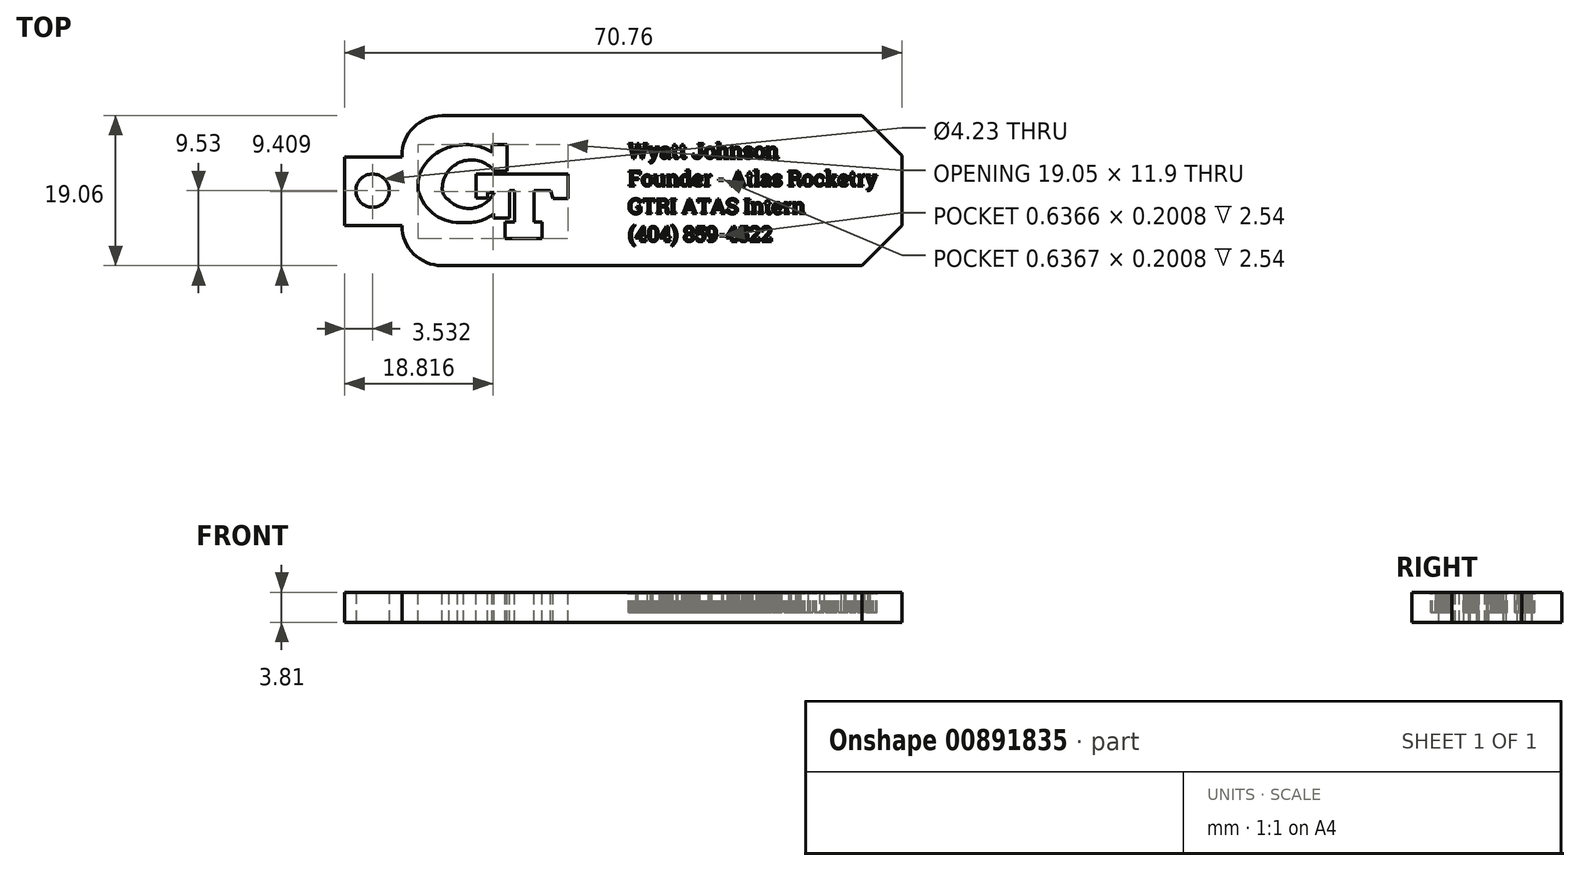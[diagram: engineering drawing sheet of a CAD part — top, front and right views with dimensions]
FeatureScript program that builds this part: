
annotation { "Feature Type Name" : "Feature", "Feature Type Description" : "" }
export const myFeature = defineFeature(function(context is Context, id is Id, definition is map)
    precondition{}
    {
        {
            var Q0;
            Q0=qCreatedBy(makeId("Top.planeOp"),FACE);
            var sketch = newSketch(context, id + "F0", { "sketchPlane" : qUnion([Q0])});
            skLineSegment(sketch, "E0.bottom", {"start": v(31.75, -9.52) * mm, "end": v(-31.75, -9.53) * mm});
            skLineSegment(sketch, "E0.top", {"start": v(31.75, 9.53) * mm, "end": v(-31.75, 9.53) * mm});
            skLineSegment(sketch, "E0.left", {"start": v(31.75, -9.53) * mm, "end": v(31.75, 9.53) * mm});
            skLineSegment(sketch, "E0.right", {"start": v(-31.75, -9.53) * mm, "end": v(-31.75, 9.53) * mm});
            skPoint(sketch, "E0.middle", {"position": v(0, 0) * mm});
            skSolve(sketch);
        }
        {
            var Q0;
            Q0 = qSketchRegion(id + "F0", true);
            var Q1;
            Q1 = qSketchRegion(id + "F8", true);
            extrude(context, id + "F1", {"entities" : qUnion([Q0, Q1]), "depth" : 3.8 * mm, "offsetDistance" : 25.4 * mm});
        }
        {
            var Q0;
            Q0=qCreatedBy(makeId("Top.planeOp"),FACE);
            var sketch = newSketch(context, id + "F2", { "sketchPlane" : qUnion([Q0])});
            skLineSegment(sketch, "E1", {"start": v(-20.28, 5.83) * mm, "end": v(-20.28, 4.88) * mm});
            skPoint(sketch, "E1.startSnap0", {"position": v(-20.28, 6.07) * mm});
            skArc(sketch, "E2", {"start": v(-28.9, 3.23) * mm, "mid": v(-29.6, 1.7) * mm, "end": v(-29.67, 0) * mm});
            skArc(sketch, "E3", {"start": v(-24.69, 5.74) * mm, "mid": v(-27.06, 4.94) * mm, "end": v(-28.9, 3.23) * mm});
            skArc(sketch, "E4", {"start": v(-20.28, 4.88) * mm, "mid": v(-22.4, 5.71) * mm, "end": v(-24.69, 5.74) * mm});
            skLineSegment(sketch, "E5", {"start": v(-20.28, 5.83) * mm, "end": v(-18.38, 5.83) * mm});
            skLineSegment(sketch, "E6", {"start": v(-18.38, 5.83) * mm, "end": v(-18.38, 2.5) * mm});
            skLineSegment(sketch, "E7", {"start": v(-18.38, 2.5) * mm, "end": v(-20.03, 2.5) * mm});
            skArc(sketch, "E8", {"start": v(-26.63, 0.26) * mm, "mid": v(-26.4, -0.6) * mm, "end": v(-25.78, -1.22) * mm});
            skArc(sketch, "E9", {"start": v(-20.03, 2.5) * mm, "mid": v(-24.12, 3.7) * mm, "end": v(-26.63, 0.26) * mm});
            skArc(sketch, "E10", {"start": v(-25.78, -1.22) * mm, "mid": v(-22.64, -2.22) * mm, "end": v(-20.03, -0.22) * mm});
            skLineSegment(sketch, "E11", {"start": v(-22.33, -0.97) * mm, "end": v(-22.33, 2.11) * mm});
            skLineSegment(sketch, "E12", {"start": v(-22.33, 2.11) * mm, "end": v(-10.67, 2.11) * mm});
            skLineSegment(sketch, "E13", {"start": v(-10.67, 2.11) * mm, "end": v(-10.67, -1.01) * mm});
            skLineSegment(sketch, "E14", {"start": v(-10.67, -1.01) * mm, "end": v(-12.54, -1.01) * mm});
            skLineSegment(sketch, "E15", {"start": v(-12.54, -1.01) * mm, "end": v(-12.9, 0) * mm});
            skLineSegment(sketch, "E16", {"start": v(-14.96, 0) * mm, "end": v(-14.96, -3.99) * mm});
            skLineSegment(sketch, "E17", {"start": v(-14.96, -3.99) * mm, "end": v(-13.96, -3.99) * mm});
            skLineSegment(sketch, "E18", {"start": v(-13.96, -3.99) * mm, "end": v(-13.96, -6.07) * mm});
            skLineSegment(sketch, "E19", {"start": v(-13.96, -6.07) * mm, "end": v(-18.64, -6.07) * mm});
            skLineSegment(sketch, "E20", {"start": v(-18.64, -6.07) * mm, "end": v(-18.64, -3.99) * mm});
            skLineSegment(sketch, "E21", {"start": v(-18.64, -3.99) * mm, "end": v(-17.44, -3.99) * mm});
            skLineSegment(sketch, "E22", {"start": v(-17.44, -3.99) * mm, "end": v(-17.44, 0) * mm});
            skLineSegment(sketch, "E23", {"start": v(-18.06, 0) * mm, "end": v(-18.06, -3.46) * mm});
            skLineSegment(sketch, "E24", {"start": v(-18.06, -3.46) * mm, "end": v(-20.09, -3.46) * mm});
            skLineSegment(sketch, "E25", {"start": v(-20.09, -3.46) * mm, "end": v(-20.09, -2.93) * mm});
            skArc(sketch, "E26", {"start": v(-29.67, 0) * mm, "mid": v(-27.53, -3.1) * mm, "end": v(-23.9, -4.05) * mm});
            skArc(sketch, "E27", {"start": v(-23.9, -4.05) * mm, "mid": v(-21.88, -3.86) * mm, "end": v(-20.09, -2.93) * mm});
            skLineSegment(sketch, "E28", {"start": v(-20.03, -0.22) * mm, "end": v(-20.84, -0.22) * mm});
            skLineSegment(sketch, "E29", {"start": v(-20.84, -0.22) * mm, "end": v(-20.84, -0.91) * mm});
            skLineSegment(sketch, "E30", {"start": v(-20.84, -0.91) * mm, "end": v(-22.33, -0.97) * mm});
            skLineSegment(sketch, "E31", {"start": v(-18.06, 0) * mm, "end": v(-17.44, 0) * mm});
            skLineSegment(sketch, "E32", {"start": v(-14.96, 0) * mm, "end": v(-12.9, 0) * mm});
            skSolve(sketch);
        }
        {
            var Q0;
            Q0 = qSketchRegion(id + "F2", true);
            extrude(context, id + "F3", {"entities" : qUnion([Q0]), "operationType" : NewBodyOperationType.REMOVE, "endBound" : BoundingType.THROUGH_ALL, "oppositeDirection" : true, "depth" : 25.4 * mm, "offsetDistance" : 25.4 * mm, "hasSecondDirection" : true, "secondDirectionOppositeDirection" : false, "secondDirectionDepth" : 25.4 * mm});
        }
        {
            var Q0;
            Q0=makeQuery(id+"F1.opExtrude","SWEPT_EDGE",EDGE,{"disambiguationData":[OSD([sQuery(id+"F0.wireOp",EDGE,"E0.bottom"),sQuery(id+"F0.wireOp",EDGE,"E0.left")])]});
            var Q1;
            Q1=makeQuery(id+"F1.opExtrude","SWEPT_EDGE",EDGE,{"disambiguationData":[OSD([sQuery(id+"F0.wireOp",EDGE,"E0.top"),sQuery(id+"F0.wireOp",EDGE,"E0.left")])]});
            chamfer(context, id + "F4", {"entities" : qUnion([Q0, Q1]), "width" : 5.08 * mm, "tangentPropagation" : true});
        }
        {
            var Q0;
            Q0=makeQuery(id+"F1.opExtrude","SWEPT_EDGE",EDGE,{"disambiguationData":[OSD([sQuery(id+"F0.wireOp",EDGE,"E0.bottom"),sQuery(id+"F0.wireOp",EDGE,"E0.right")])]});
            var Q1;
            Q1=makeQuery(id+"F1.opExtrude","SWEPT_EDGE",EDGE,{"disambiguationData":[OSD([sQuery(id+"F0.wireOp",EDGE,"E0.top"),sQuery(id+"F0.wireOp",EDGE,"E0.right")])]});
            fillet(context, id + "F5", {"entities" : qUnion([Q0, Q1]), "radius" : 5.08 * mm, "tangentPropagation" : true, "allowEdgeOverflow" : false});
        }
        {
            var Q0;
            Q0=makeQuery(id+"F1.opExtrude","CAP_FACE",FACE,{"disambiguationData":[OSD([sQuery(id+"F0.wireOp",EDGE,"E0.bottom"),sQuery(id+"F0.wireOp",EDGE,"E0.top"),sQuery(id+"F0.wireOp",EDGE,"E0.left"),sQuery(id+"F0.wireOp",EDGE,"E0.right")])],"isStart":false});
            var sketch = newSketch(context, id + "F6", { "sketchPlane" : qUnion([Q0])});
            skText(sketch, "E33", { "text": "Wyatt Johnson \nFounder - Atlas Rocketry \nGTRI ATAS Intern\n(404) 859-4522", "fontName": "RobotoSlab-Regular.ttf"});
            const initialGuessF6  = {"E33": [-0.003, 0.0041, 1, 0, 0.00192]};
            skSetInitialGuess(sketch, initialGuessF6);
            skSolve(sketch);
        }
        {
            var Q0;
            Q0 = qSketchRegion(id + "F6", true);
            extrude(context, id + "F7", {"entities" : qUnion([Q0]), "operationType" : NewBodyOperationType.REMOVE, "oppositeDirection" : true, "depth" : 2.54 * mm, "offsetDistance" : 25.4 * mm});
        }
        {
            var Q0;
            Q0=makeQuery(id+"F1.opExtrude","CAP_FACE",FACE,{"disambiguationData":[OSD([sQuery(id+"F0.wireOp",EDGE,"E0.bottom"),sQuery(id+"F0.wireOp",EDGE,"E0.top"),sQuery(id+"F0.wireOp",EDGE,"E0.left"),sQuery(id+"F0.wireOp",EDGE,"E0.right")])],"isStart":true});
            var sketch = newSketch(context, id + "F8", { "sketchPlane" : qUnion([Q0])});
            skLineSegment(sketch, "E34.bottom", {"start": v(-31.75, 4.45) * mm, "end": v(-39.01, 4.45) * mm});
            skLineSegment(sketch, "E34.top", {"start": v(-31.75, -4.24) * mm, "end": v(-39.01, -4.24) * mm});
            skLineSegment(sketch, "E34.left", {"start": v(-31.75, 4.45) * mm, "end": v(-31.75, -4.24) * mm});
            skLineSegment(sketch, "E34.right", {"start": v(-39.01, 4.45) * mm, "end": v(-39.01, -4.24) * mm});
            skSolve(sketch);
        }
        {
            var Q0;
            Q0 = qSketchRegion(id + "F8", true);
            extrude(context, id + "F9", {"entities" : qUnion([Q0]), "operationType" : NewBodyOperationType.ADD, "depth" : 0 * mm, "offsetDistance" : 25.4 * mm, "hasSecondDirection" : true, "secondDirectionOppositeDirection" : true, "secondDirectionDepth" : 3.8 * mm});
        }
        {
            var Q0;
            Q0=makeQuery(id+"F9.boolean.opBoolean","MERGE",FACE,{"derivedFrom":[makeQuery(id+"F1.opExtrude","CAP_FACE",FACE,{"disambiguationData":[OSD([sQuery(id+"F0.wireOp",EDGE,"E0.bottom"),sQuery(id+"F0.wireOp",EDGE,"E0.top"),sQuery(id+"F0.wireOp",EDGE,"E0.left"),sQuery(id+"F0.wireOp",EDGE,"E0.right")])],"isStart":true}),makeQuery(id+"F9.opExtrude","CAP_FACE",FACE,{"disambiguationData":[OSD([sQuery(id+"F8.wireOp",EDGE,"E34.bottom"),sQuery(id+"F8.wireOp",EDGE,"E34.top"),sQuery(id+"F8.wireOp",EDGE,"E34.left"),sQuery(id+"F8.wireOp",EDGE,"E34.right")])],"isStart":false})]});
            var sketch = newSketch(context, id + "F10", { "sketchPlane" : qUnion([Q0])});
            skCircle(sketch, "E35", {"center": v(-35.48, 0) * mm, "radius": 2.11 * mm});
            skSolve(sketch);
        }
        {
            var Q0;
            Q0 = qSketchRegion(id + "F10", true);
            extrude(context, id + "F11", {"entities" : qUnion([Q0]), "operationType" : NewBodyOperationType.REMOVE, "oppositeDirection" : true, "depth" : 25.4 * mm, "offsetDistance" : 25.4 * mm, "hasSecondDirection" : true, "secondDirectionOppositeDirection" : false, "secondDirectionDepth" : 25.4 * mm});
        }
    });
